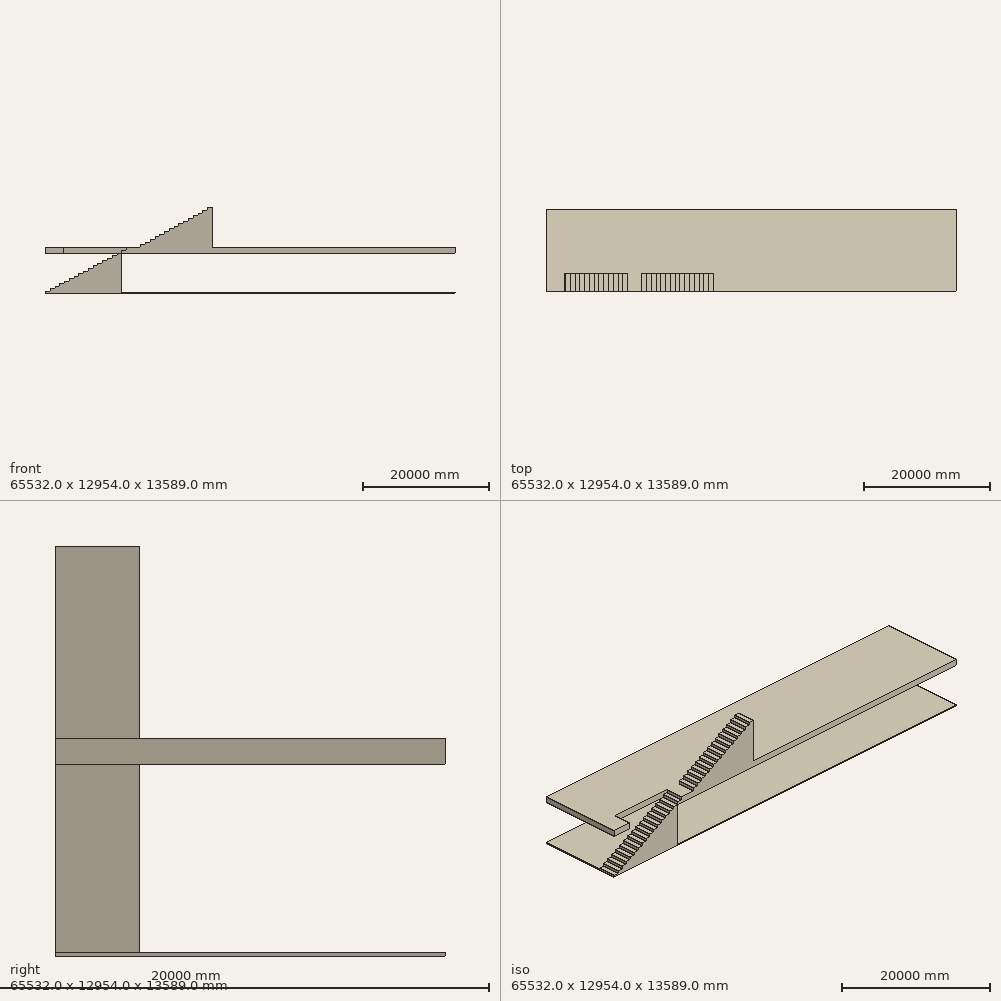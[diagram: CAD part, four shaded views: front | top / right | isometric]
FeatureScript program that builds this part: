
annotation { "Feature Type Name" : "Feature", "Feature Type Description" : "" }
export const myFeature = defineFeature(function(context is Context, id is Id, definition is map)
    precondition{}
    {
        {
            var Q0;
            Q0=qCreatedBy(makeId("Front.planeOp"),FACE);
            var sketch = newSketch(context, id + "F0", { "sketchPlane" : qUnion([Q0])});
            skLineSegment(sketch, "E0", {"start": v(-10856.47, -4724.4) * mm, "end": v(1335.53, -4724.4) * mm});
            skLineSegment(sketch, "E1", {"start": v(1335.53, -4724.4) * mm, "end": v(1335.53, 1625.6) * mm});
            skLineSegment(sketch, "E2", {"start": v(1335.53, 1625.6) * mm, "end": v(573.53, 1625.6) * mm});
            skLineSegment(sketch, "E3", {"start": v(573.53, 1625.6) * mm, "end": v(573.53, 1219.2) * mm});
            skLineSegment(sketch, "E4", {"start": v(573.53, 1219.2) * mm, "end": v(-188.47, 1219.2) * mm});
            skLineSegment(sketch, "E5", {"start": v(-188.47, 1219.2) * mm, "end": v(-188.47, 812.8) * mm});
            skLineSegment(sketch, "E6", {"start": v(-188.47, 812.8) * mm, "end": v(-950.47, 812.8) * mm});
            skLineSegment(sketch, "E7", {"start": v(-950.47, 812.8) * mm, "end": v(-950.47, 406.4) * mm});
            skLineSegment(sketch, "E8", {"start": v(-950.47, 406.4) * mm, "end": v(-1712.47, 406.4) * mm});
            skLineSegment(sketch, "E9", {"start": v(-1712.47, 406.4) * mm, "end": v(-1712.47, 0) * mm});
            skLineSegment(sketch, "E10", {"start": v(-1712.47, 0) * mm, "end": v(-2474.47, 0) * mm});
            skLineSegment(sketch, "E11", {"start": v(-2474.47, 0) * mm, "end": v(-2474.47, -406.4) * mm});
            skLineSegment(sketch, "E12", {"start": v(-2474.47, -406.4) * mm, "end": v(-3236.47, -406.4) * mm});
            skLineSegment(sketch, "E13", {"start": v(-3236.47, -406.4) * mm, "end": v(-3236.47, -812.8) * mm});
            skLineSegment(sketch, "E14", {"start": v(-3236.47, -812.8) * mm, "end": v(-3998.47, -812.8) * mm});
            skLineSegment(sketch, "E15", {"start": v(-3998.47, -812.8) * mm, "end": v(-3998.47, -1219.2) * mm});
            skLineSegment(sketch, "E16", {"start": v(-3998.47, -1219.2) * mm, "end": v(-4760.47, -1219.2) * mm});
            skLineSegment(sketch, "E17", {"start": v(-4760.47, -1219.2) * mm, "end": v(-4760.47, -1625.6) * mm});
            skLineSegment(sketch, "E18", {"start": v(-4760.47, -1625.6) * mm, "end": v(-5522.47, -1625.6) * mm});
            skLineSegment(sketch, "E19", {"start": v(-5522.47, -1625.6) * mm, "end": v(-5522.47, -2032) * mm});
            skLineSegment(sketch, "E20", {"start": v(-5522.47, -2032) * mm, "end": v(-6284.47, -2032) * mm});
            skLineSegment(sketch, "E21", {"start": v(-6284.47, -2032) * mm, "end": v(-6284.47, -2438.4) * mm});
            skLineSegment(sketch, "E22", {"start": v(-6284.47, -2438.4) * mm, "end": v(-7046.47, -2438.4) * mm});
            skLineSegment(sketch, "E23", {"start": v(-7046.47, -2438.4) * mm, "end": v(-7046.47, -2844.8) * mm});
            skLineSegment(sketch, "E24", {"start": v(-7046.47, -2844.8) * mm, "end": v(-7808.47, -2844.8) * mm});
            skLineSegment(sketch, "E25", {"start": v(-7808.47, -2844.8) * mm, "end": v(-7808.47, -3251.2) * mm});
            skLineSegment(sketch, "E26", {"start": v(-7808.47, -3251.2) * mm, "end": v(-8570.47, -3251.2) * mm});
            skLineSegment(sketch, "E27", {"start": v(-8570.47, -3251.2) * mm, "end": v(-8570.47, -3657.6) * mm});
            skLineSegment(sketch, "E28", {"start": v(-8570.47, -3657.6) * mm, "end": v(-9332.47, -3657.6) * mm});
            skLineSegment(sketch, "E29", {"start": v(-9332.47, -3657.6) * mm, "end": v(-9332.47, -4064) * mm});
            skLineSegment(sketch, "E30", {"start": v(-9332.47, -4064) * mm, "end": v(-10094.47, -4064) * mm});
            skLineSegment(sketch, "E31", {"start": v(-10094.47, -4064) * mm, "end": v(-10094.47, -4470.4) * mm});
            skLineSegment(sketch, "E32", {"start": v(-10856.47, -4724.4) * mm, "end": v(-10856.47, -4470.4) * mm});
            skLineSegment(sketch, "E33", {"start": v(-10856.47, -4470.4) * mm, "end": v(-10094.47, -4470.4) * mm});
            skSolve(sketch);
        }
        {
            var Q0;
            Q0=makeQuery(id+"F0.imprint","IMPRINT",FACE,{"disambiguationData":[TD([[makeQuery(id+"F0.imprint","IMPRINT",EDGE,{"derivedFrom":sQuery(id+"F0.wireOp",EDGE,"E0")}),1.0]])]});
            extrude(context, id + "F1", {"entities" : qUnion([Q0]), "depth" : 2794 * mm});
        }
        {
            var Q0;
            Q0=makeQuery(id+"F1.opExtrude","CAP_FACE",FACE,{"disambiguationData":[OSD([sQuery(id+"F0.wireOp",EDGE,"E0"),sQuery(id+"F0.wireOp",EDGE,"E1"),sQuery(id+"F0.wireOp",EDGE,"E2"),sQuery(id+"F0.wireOp",EDGE,"E3"),sQuery(id+"F0.wireOp",EDGE,"E4"),sQuery(id+"F0.wireOp",EDGE,"E5"),sQuery(id+"F0.wireOp",EDGE,"E6"),sQuery(id+"F0.wireOp",EDGE,"E7"),sQuery(id+"F0.wireOp",EDGE,"E8"),sQuery(id+"F0.wireOp",EDGE,"E9"),sQuery(id+"F0.wireOp",EDGE,"E10"),sQuery(id+"F0.wireOp",EDGE,"E11"),sQuery(id+"F0.wireOp",EDGE,"E12"),sQuery(id+"F0.wireOp",EDGE,"E13"),sQuery(id+"F0.wireOp",EDGE,"E14"),sQuery(id+"F0.wireOp",EDGE,"E15"),sQuery(id+"F0.wireOp",EDGE,"E16"),sQuery(id+"F0.wireOp",EDGE,"E17"),sQuery(id+"F0.wireOp",EDGE,"E18"),sQuery(id+"F0.wireOp",EDGE,"E19"),sQuery(id+"F0.wireOp",EDGE,"E20"),sQuery(id+"F0.wireOp",EDGE,"E21"),sQuery(id+"F0.wireOp",EDGE,"E22"),sQuery(id+"F0.wireOp",EDGE,"E23"),sQuery(id+"F0.wireOp",EDGE,"E24"),sQuery(id+"F0.wireOp",EDGE,"E25"),sQuery(id+"F0.wireOp",EDGE,"E26"),sQuery(id+"F0.wireOp",EDGE,"E27"),sQuery(id+"F0.wireOp",EDGE,"E28"),sQuery(id+"F0.wireOp",EDGE,"E29"),sQuery(id+"F0.wireOp",EDGE,"E30"),sQuery(id+"F0.wireOp",EDGE,"E31"),sQuery(id+"F0.wireOp",EDGE,"E32"),sQuery(id+"F0.wireOp",EDGE,"E33")])],"isStart":true});
            var sketch = newSketch(context, id + "F2", { "sketchPlane" : qUnion([Q0])});
            skLineSegment(sketch, "E34", {"start": v(-1335.53, -4724.4) * mm, "end": v(-1335.53, -4597.4) * mm});
            skLineSegment(sketch, "E35", {"start": v(-1335.53, -4597.4) * mm, "end": v(10856.47, -4597.4) * mm});
            skLineSegment(sketch, "E36", {"start": v(10856.47, -4597.4) * mm, "end": v(10856.47, -4724.4) * mm});
            skLineSegment(sketch, "E37", {"start": v(10856.47, -4724.4) * mm, "end": v(-1335.53, -4724.4) * mm});
            skSolve(sketch);
        }
        {
            var Q0;
            Q0 = qSketchRegion(id + "F2", true);
            extrude(context, id + "F3", {"entities" : qUnion([Q0]), "operationType" : NewBodyOperationType.ADD, "depth" : 10160 * mm});
        }
        {
            var Q0;
            Q0=makeQuery(id+"F3.boolean.opBoolean","MERGE",FACE,{"derivedFrom":[makeQuery(id+"F1.opExtrude","SWEPT_FACE",FACE,{"disambiguationData":[OSD([sQuery(id+"F0.wireOp",EDGE,"E1")])]}),makeQuery(id+"F3.opExtrude","SWEPT_FACE",FACE,{"disambiguationData":[OSD([sQuery(id+"F2.wireOp",EDGE,"E34")])]})]});
            var sketch = newSketch(context, id + "F4", { "sketchPlane" : qUnion([Q0])});
            skLineSegment(sketch, "E38.bottom", {"start": v(-2794, -4724.4) * mm, "end": v(10160, -4724.4) * mm});
            skLineSegment(sketch, "E38.top", {"start": v(-2794, -4597.4) * mm, "end": v(10160, -4597.4) * mm});
            skLineSegment(sketch, "E38.left", {"start": v(-2794, -4724.4) * mm, "end": v(-2794, -4597.4) * mm});
            skLineSegment(sketch, "E38.right", {"start": v(10160, -4724.4) * mm, "end": v(10160, -4597.4) * mm});
            skSolve(sketch);
        }
        {
            var Q0;
            Q0=makeQuery(id+"F4.imprint","IMPRINT",FACE,{"disambiguationData":[TD([[makeQuery(id+"F4.imprint","IMPRINT",EDGE,{"derivedFrom":sQuery(id+"F4.wireOp",EDGE,"E38.bottom")}),1.0]])]});
            extrude(context, id + "F5", {"entities" : qUnion([Q0]), "operationType" : NewBodyOperationType.ADD, "depth" : 53340 * mm});
        }
        {
            var Q0;
            Q0=makeQuery(id+"F1.opExtrude","SWEPT_FACE",FACE,{"disambiguationData":[OSD([sQuery(id+"F0.wireOp",EDGE,"E2")])]});
            var sketch = newSketch(context, id + "F6", { "sketchPlane" : qUnion([Q0])});
            skLineSegment(sketch, "E39.bottom", {"start": v(-10856.47, 10160) * mm, "end": v(54675.53, 10160) * mm});
            skLineSegment(sketch, "E39.top", {"start": v(-10856.47, -2794) * mm, "end": v(54675.53, -2794) * mm});
            skLineSegment(sketch, "E39.left", {"start": v(-10856.47, 10160) * mm, "end": v(-10856.47, -2794) * mm});
            skLineSegment(sketch, "E39.right", {"start": v(54675.53, 10160) * mm, "end": v(54675.53, -2794) * mm});
            skSolve(sketch);
        }
        {
            var Q0;
            Q0=makeQuery(id+"F6.imprint","IMPRINT",FACE,{"disambiguationData":[TD([[makeQuery(id+"F6.imprint","IMPRINT",EDGE,{"derivedFrom":sQuery(id+"F6.wireOp",EDGE,"E39.bottom")}),-1.0]])]});
            extrude(context, id + "F7", {"entities" : qUnion([Q0]), "depth" : 889 * mm});
        }
        {
            var Q0;
            Q0=makeQuery(id+"F7.opExtrude","CAP_FACE",FACE,{"disambiguationData":[OSD([sQuery(id+"F0.wireOp",EDGE,"E1"),sQuery(id+"F0.wireOp",EDGE,"E2"),sQuery(id+"F0.wireOp",EDGE,"E3"),sQuery(id+"F6.wireOp",EDGE,"E39.bottom"),sQuery(id+"F6.wireOp",EDGE,"E39.top"),sQuery(id+"F6.wireOp",EDGE,"E39.left"),sQuery(id+"F6.wireOp",EDGE,"E39.right")])],"isStart":false});
            var sketch = newSketch(context, id + "F8", { "sketchPlane" : qUnion([Q0])});
            skLineSegment(sketch, "E40.bottom", {"start": v(573.53, -2794) * mm, "end": v(-7935.47, -2794) * mm});
            skLineSegment(sketch, "E40.top", {"start": v(573.53, 0) * mm, "end": v(-7935.47, 0) * mm});
            skLineSegment(sketch, "E40.left", {"start": v(573.53, -2794) * mm, "end": v(573.53, 0) * mm});
            skLineSegment(sketch, "E40.right", {"start": v(-7935.47, -2794) * mm, "end": v(-7935.47, 0) * mm});
            skSolve(sketch);
        }
        {
            var Q0;
            Q0=makeQuery(id+"F8.imprint","IMPRINT",FACE,{"disambiguationData":[TD([[makeQuery(id+"F8.imprint","IMPRINT",EDGE,{"derivedFrom":sQuery(id+"F8.wireOp",EDGE,"E40.bottom")}),1.0]])]});
            extrude(context, id + "F9", {"entities" : qUnion([Q0]), "operationType" : NewBodyOperationType.REMOVE, "oppositeDirection" : true, "depth" : 889 * mm});
        }
        {
            var Q0;
            {var subQ0=sQuery(id+"F6.wireOp",EDGE,"E39.top");Q0=makeQuery(id+"F7.opExtrude","SWEPT_FACE",FACE,{"disambiguationData":[OSD([subQ0]),TDD([makeQuery(id+"F6.imprint","IMPRINT",EDGE,{"disambiguationData":[TD([[makeQuery(id+"F6.imprint","INTERSECT",VERTEX,{"derivedFrom":[makeQuery(id+"F1.opExtrude","SWEPT_EDGE",EDGE,{"disambiguationData":[OSD([sQuery(id+"F0.wireOp",EDGE,"E1"),sQuery(id+"F0.wireOp",EDGE,"E2")])]}),subQ0]}),-1.0],[makeQuery(id+"F6.imprint","INTERSECT",VERTEX,{"derivedFrom":[subQ0,sQuery(id+"F6.wireOp",EDGE,"E39.right")]}),1.0]])],"derivedFrom":subQ0})])]});}
            var sketch = newSketch(context, id + "F10", { "sketchPlane" : qUnion([Q0])});
            skLineSegment(sketch, "E41", {"start": v(8955.53, 5511.8) * mm, "end": v(9717.53, 5511.8) * mm});
            skLineSegment(sketch, "E42", {"start": v(9717.53, 5511.8) * mm, "end": v(9717.53, 5930.9) * mm});
            skLineSegment(sketch, "E43", {"start": v(9717.53, 5930.9) * mm, "end": v(10479.53, 5930.9) * mm});
            skLineSegment(sketch, "E44", {"start": v(10479.53, 5930.9) * mm, "end": v(10479.53, 6350) * mm});
            skLineSegment(sketch, "E45", {"start": v(10479.53, 6350) * mm, "end": v(11241.53, 6350) * mm});
            skLineSegment(sketch, "E46", {"start": v(11241.53, 6350) * mm, "end": v(11241.53, 6769.1) * mm});
            skLineSegment(sketch, "E47", {"start": v(11241.53, 6769.1) * mm, "end": v(12003.53, 6769.1) * mm});
            skLineSegment(sketch, "E48", {"start": v(12003.53, 6769.1) * mm, "end": v(12003.53, 7188.2) * mm});
            skLineSegment(sketch, "E49", {"start": v(12003.53, 7188.2) * mm, "end": v(12765.53, 7188.2) * mm});
            skLineSegment(sketch, "E50", {"start": v(12765.53, 7188.2) * mm, "end": v(12765.53, 7607.3) * mm});
            skLineSegment(sketch, "E51", {"start": v(12765.53, 7607.3) * mm, "end": v(13527.53, 7607.3) * mm});
            skLineSegment(sketch, "E52", {"start": v(13527.53, 7607.3) * mm, "end": v(13527.53, 8026.4) * mm});
            skLineSegment(sketch, "E53", {"start": v(13527.53, 8026.4) * mm, "end": v(14289.53, 8026.4) * mm});
            skLineSegment(sketch, "E54", {"start": v(14289.53, 8026.4) * mm, "end": v(14289.53, 8445.5) * mm});
            skLineSegment(sketch, "E55", {"start": v(14289.53, 8445.5) * mm, "end": v(15051.53, 8445.5) * mm});
            skLineSegment(sketch, "E56", {"start": v(15051.53, 8445.5) * mm, "end": v(15051.53, 8864.6) * mm});
            skLineSegment(sketch, "E57", {"start": v(15051.53, 8864.6) * mm, "end": v(15813.53, 8864.6) * mm});
            skLineSegment(sketch, "E58", {"start": v(15813.53, 8864.6) * mm, "end": v(15813.53, 2514.6) * mm});
            skLineSegment(sketch, "E59", {"start": v(15813.53, 2514.6) * mm, "end": v(4383.53, 2514.6) * mm});
            skLineSegment(sketch, "E60", {"start": v(4383.53, 2514.6) * mm, "end": v(1335.53, 2514.6) * mm});
            skLineSegment(sketch, "E61", {"start": v(8955.53, 5511.8) * mm, "end": v(8955.53, 5092.7) * mm});
            skLineSegment(sketch, "E62", {"start": v(8955.53, 5092.7) * mm, "end": v(8193.53, 5092.7) * mm});
            skLineSegment(sketch, "E63", {"start": v(8193.53, 5092.7) * mm, "end": v(8193.53, 4673.6) * mm});
            skLineSegment(sketch, "E64", {"start": v(8193.53, 4673.6) * mm, "end": v(7431.53, 4673.6) * mm});
            skLineSegment(sketch, "E65", {"start": v(7431.53, 4673.6) * mm, "end": v(7431.53, 4254.5) * mm});
            skLineSegment(sketch, "E66", {"start": v(7431.53, 4254.5) * mm, "end": v(6669.53, 4254.5) * mm});
            skLineSegment(sketch, "E67", {"start": v(6669.53, 4254.5) * mm, "end": v(6669.53, 3835.4) * mm});
            skLineSegment(sketch, "E68", {"start": v(6669.53, 3835.4) * mm, "end": v(5907.53, 3835.4) * mm});
            skLineSegment(sketch, "E69", {"start": v(5907.53, 3835.4) * mm, "end": v(5907.53, 3416.3) * mm});
            skLineSegment(sketch, "E70", {"start": v(5907.53, 3416.3) * mm, "end": v(5145.53, 3416.3) * mm});
            skLineSegment(sketch, "E71", {"start": v(5145.53, 3416.3) * mm, "end": v(5145.53, 2997.2) * mm});
            skLineSegment(sketch, "E72", {"start": v(5145.53, 2997.2) * mm, "end": v(4383.53, 2997.2) * mm});
            skLineSegment(sketch, "E73", {"start": v(4383.53, 2997.2) * mm, "end": v(4383.53, 2514.6) * mm});
            skSolve(sketch);
        }
        {
            var Q0;
            Q0=makeQuery(id+"F10.imprint","IMPRINT",FACE,{"disambiguationData":[TD([[makeQuery(id+"F10.imprint","IMPRINT",EDGE,{"derivedFrom":sQuery(id+"F10.wireOp",EDGE,"E41")}),-1.0]])]});
            extrude(context, id + "F11", {"entities" : qUnion([Q0]), "operationType" : NewBodyOperationType.ADD, "oppositeDirection" : true, "depth" : 2794 * mm});
        }
        {
            var Q0;
            {var subQ0=sQuery(id+"F6.wireOp",EDGE,"E39.top");Q0=makeQuery(id+"F11.boolean.opBoolean","MERGE",FACE,{"derivedFrom":[makeQuery(id+"F7.opExtrude","SWEPT_FACE",FACE,{"disambiguationData":[OSD([subQ0]),TDD([makeQuery(id+"F6.imprint","IMPRINT",EDGE,{"disambiguationData":[TD([[makeQuery(id+"F6.imprint","INTERSECT",VERTEX,{"derivedFrom":[makeQuery(id+"F1.opExtrude","SWEPT_EDGE",EDGE,{"disambiguationData":[OSD([sQuery(id+"F0.wireOp",EDGE,"E1"),sQuery(id+"F0.wireOp",EDGE,"E2")])]}),subQ0]}),-1.0],[makeQuery(id+"F6.imprint","INTERSECT",VERTEX,{"derivedFrom":[subQ0,sQuery(id+"F6.wireOp",EDGE,"E39.right")]}),1.0]])],"derivedFrom":subQ0})])]}),makeQuery(id+"F11.opExtrude","CAP_FACE",FACE,{"disambiguationData":[OSD([sQuery(id+"F10.wireOp",EDGE,"E41"),sQuery(id+"F10.wireOp",EDGE,"E42"),sQuery(id+"F10.wireOp",EDGE,"E43"),sQuery(id+"F10.wireOp",EDGE,"E44"),sQuery(id+"F10.wireOp",EDGE,"E45"),sQuery(id+"F10.wireOp",EDGE,"E46"),sQuery(id+"F10.wireOp",EDGE,"E47"),sQuery(id+"F10.wireOp",EDGE,"E48"),sQuery(id+"F10.wireOp",EDGE,"E49"),sQuery(id+"F10.wireOp",EDGE,"E50"),sQuery(id+"F10.wireOp",EDGE,"E51"),sQuery(id+"F10.wireOp",EDGE,"E52"),sQuery(id+"F10.wireOp",EDGE,"E53"),sQuery(id+"F10.wireOp",EDGE,"E54"),sQuery(id+"F10.wireOp",EDGE,"E55"),sQuery(id+"F10.wireOp",EDGE,"E56"),sQuery(id+"F10.wireOp",EDGE,"E57"),sQuery(id+"F10.wireOp",EDGE,"E58"),sQuery(id+"F10.wireOp",EDGE,"E59"),sQuery(id+"F10.wireOp",EDGE,"E61"),sQuery(id+"F10.wireOp",EDGE,"E62"),sQuery(id+"F10.wireOp",EDGE,"E63"),sQuery(id+"F10.wireOp",EDGE,"E64"),sQuery(id+"F10.wireOp",EDGE,"E65"),sQuery(id+"F10.wireOp",EDGE,"E66"),sQuery(id+"F10.wireOp",EDGE,"E67"),sQuery(id+"F10.wireOp",EDGE,"E68"),sQuery(id+"F10.wireOp",EDGE,"E69"),sQuery(id+"F10.wireOp",EDGE,"E70"),sQuery(id+"F10.wireOp",EDGE,"E71"),sQuery(id+"F10.wireOp",EDGE,"E72"),sQuery(id+"F10.wireOp",EDGE,"E73")])],"isStart":true})]});}
            var sketch = newSketch(context, id + "F12", { "sketchPlane" : qUnion([Q0])});
            skLineSegment(sketch, "E74", {"start": v(1335.53, 2057.4) * mm, "end": v(2097.53, 2057.4) * mm});
            skLineSegment(sketch, "E75", {"start": v(2097.53, 2057.4) * mm, "end": v(2097.53, 2514.6) * mm});
            skLineSegment(sketch, "E76", {"start": v(2097.53, 2514.6) * mm, "end": v(1335.53, 2514.6) * mm});
            skLineSegment(sketch, "E77", {"start": v(1335.53, 2514.6) * mm, "end": v(1335.53, 2057.4) * mm});
            skLineSegment(sketch, "E78", {"start": v(1335.53, 2057.4) * mm, "end": v(1335.53, 1625.6) * mm});
            skSolve(sketch);
        }
        {
            var Q0;
            Q0=makeQuery(id+"F12.imprint","IMPRINT",FACE,{"disambiguationData":[TD([[makeQuery(id+"F12.imprint","IMPRINT",EDGE,{"derivedFrom":sQuery(id+"F12.wireOp",EDGE,"E74")}),1.0]])]});
            extrude(context, id + "F13", {"entities" : qUnion([Q0]), "operationType" : NewBodyOperationType.REMOVE, "oppositeDirection" : true, "depth" : 2794 * mm});
        }
    });
